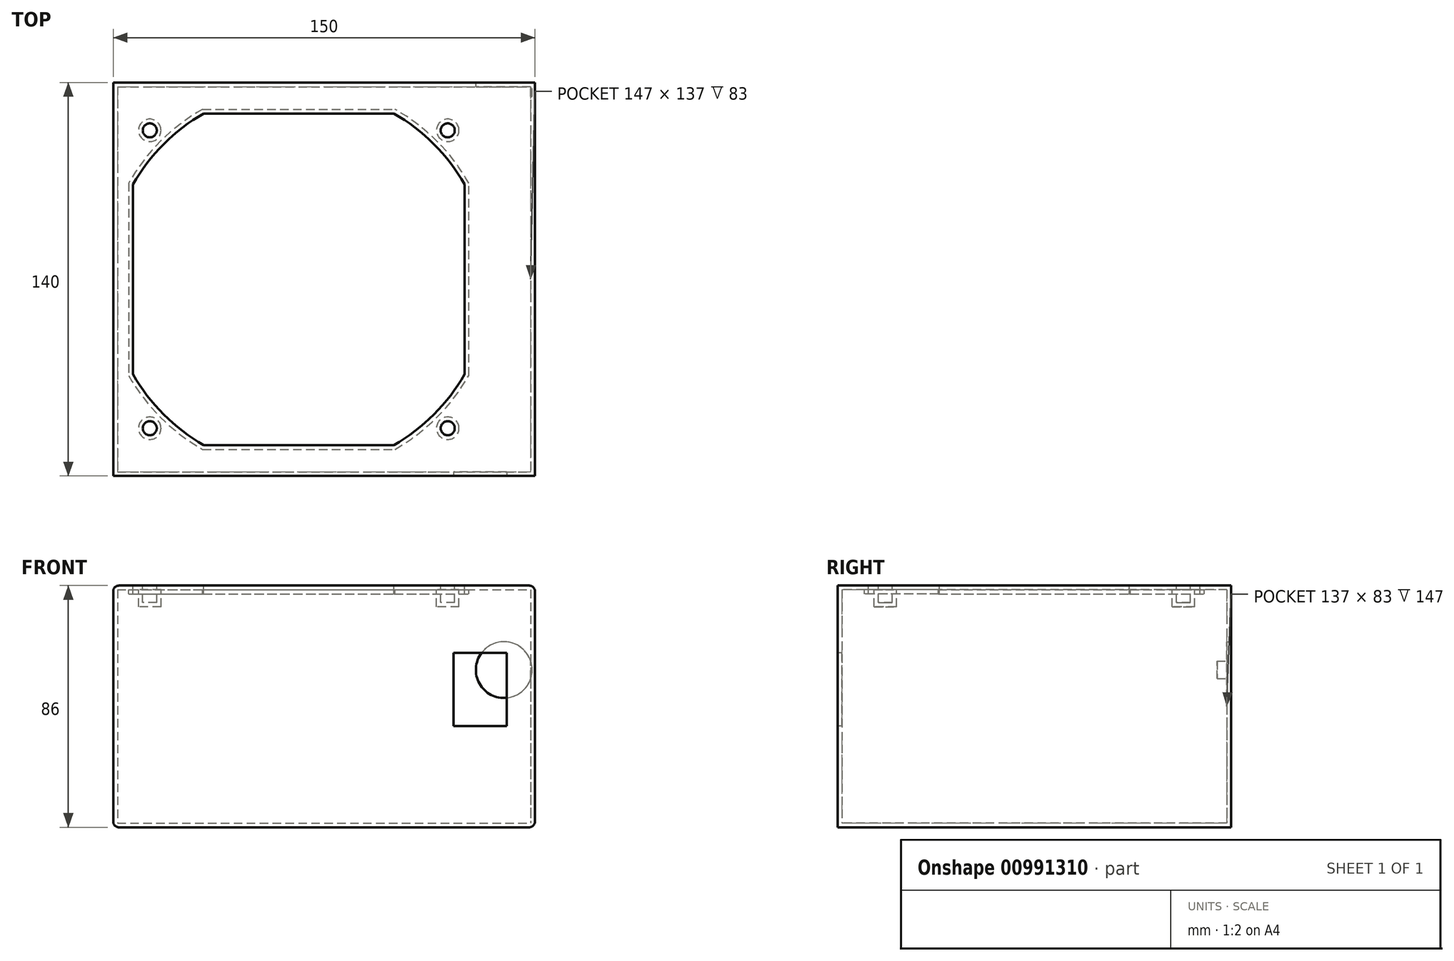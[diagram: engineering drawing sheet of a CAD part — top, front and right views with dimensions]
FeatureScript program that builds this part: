
annotation { "Feature Type Name" : "Feature", "Feature Type Description" : "" }
export const myFeature = defineFeature(function(context is Context, id is Id, definition is map)
    precondition{}
    {
        {
            var Q0;
            Q0=qCreatedBy(makeId("Top.planeOp"),FACE);
            var sketch = newSketch(context, id + "F0", { "sketchPlane" : qUnion([Q0])});
            skLineSegment(sketch, "E0.bottom", {"start": v(-75, 70) * mm, "end": v(75, 70) * mm});
            skLineSegment(sketch, "E0.top", {"start": v(-75, -70) * mm, "end": v(75, -70) * mm});
            skLineSegment(sketch, "E0.left", {"start": v(-75, 70) * mm, "end": v(-75, -70) * mm});
            skLineSegment(sketch, "E0.right", {"start": v(75, 70) * mm, "end": v(75, -70) * mm});
            skPoint(sketch, "E0.middle", {"position": v(0, 0) * mm});
            skSolve(sketch);
        }
        {
            var Q0;
            Q0 = qSketchRegion(id + "F0", true);
            extrude(context, id + "F1", {"entities" : qUnion([Q0]), "depth" : 86 * mm, "offsetDistance" : 25 * mm});
        }
        {
            var Q0;
            Q0=makeQuery(id+"F1.opExtrude","CAP_FACE",FACE,{"disambiguationData":[OSD([sQuery(id+"F0.wireOp",EDGE,"E0.bottom"),sQuery(id+"F0.wireOp",EDGE,"E0.top"),sQuery(id+"F0.wireOp",EDGE,"E0.left"),sQuery(id+"F0.wireOp",EDGE,"E0.right")])],"isStart":false});
            var sketch = newSketch(context, id + "F2", { "sketchPlane" : qUnion([Q0])});
            skCircle(sketch, "E1", {"center": v(44, -53) * mm, "radius": 2.5 * mm});
            skCircle(sketch, "E2", {"center": v(-62, 53) * mm, "radius": 2.5 * mm});
            skCircle(sketch, "E3", {"center": v(44, 53) * mm, "radius": 2.5 * mm});
            skCircle(sketch, "E4", {"center": v(-62, -53) * mm, "radius": 2.5 * mm});
            skLineSegment(sketch, "E5", {"start": v(-9, 0) * mm, "end": v(-62, -53) * mm, "construction": true});
            skArc(sketch, "E6", {"start": v(-42.8, 59) * mm, "mid": v(-57.08, 48.08) * mm, "end": v(-68, 33.8) * mm});
            skArc(sketch, "E7.1.0", {"start": v(-68, -33.8) * mm, "mid": v(-57.08, -48.08) * mm, "end": v(-42.8, -59) * mm});
            skArc(sketch, "E7.2.0", {"start": v(24.8, -59) * mm, "mid": v(39.08, -48.08) * mm, "end": v(50, -33.8) * mm});
            skArc(sketch, "E7.3.0", {"start": v(50, 33.8) * mm, "mid": v(39.08, 48.08) * mm, "end": v(24.8, 59) * mm});
            skLineSegment(sketch, "E8", {"start": v(-68, 33.8) * mm, "end": v(-68, -33.8) * mm});
            skLineSegment(sketch, "E9", {"start": v(-42.8, -59) * mm, "end": v(24.8, -59) * mm});
            skLineSegment(sketch, "E10", {"start": v(50, -33.8) * mm, "end": v(50, 33.8) * mm});
            skLineSegment(sketch, "E11", {"start": v(-42.8, 59) * mm, "end": v(24.8, 59) * mm});
            skSolve(sketch);
        }
        {
            var Q0;
            Q0=makeQuery(id+"F2.imprint","IMPRINT",FACE,{"disambiguationData":[TD([[makeQuery(id+"F2.imprint","IMPRINT",EDGE,{"derivedFrom":sQuery(id+"F2.wireOp",EDGE,"E6")}),1.0]])]});
            extrude(context, id + "F3", {"entities" : qUnion([Q0]), "operationType" : NewBodyOperationType.REMOVE, "oppositeDirection" : true, "depth" : 3 * mm, "offsetDistance" : 25 * mm});
        }
        {
            var Q0;
            Q0=makeQuery(id+"F2.imprint","IMPRINT",FACE,{"disambiguationData":[TD([[makeQuery(id+"F2.imprint","IMPRINT",EDGE,{"derivedFrom":sQuery(id+"F2.wireOp",EDGE,"E2")}),1.0]])]});
            var Q1;
            Q1=makeQuery(id+"F2.imprint","IMPRINT",FACE,{"disambiguationData":[TD([[makeQuery(id+"F2.imprint","IMPRINT",EDGE,{"derivedFrom":sQuery(id+"F2.wireOp",EDGE,"E3")}),1.0]])]});
            var Q2;
            Q2=makeQuery(id+"F2.imprint","IMPRINT",FACE,{"disambiguationData":[TD([[makeQuery(id+"F2.imprint","IMPRINT",EDGE,{"derivedFrom":sQuery(id+"F2.wireOp",EDGE,"E1")}),1.0]])]});
            var Q3;
            Q3=makeQuery(id+"F2.imprint","IMPRINT",FACE,{"disambiguationData":[TD([[makeQuery(id+"F2.imprint","IMPRINT",EDGE,{"derivedFrom":sQuery(id+"F2.wireOp",EDGE,"E4")}),1.0]])]});
            extrude(context, id + "F4", {"entities" : qUnion([Q0, Q1, Q2, Q3]), "operationType" : NewBodyOperationType.REMOVE, "oppositeDirection" : true, "depth" : 6 * mm, "offsetDistance" : 25 * mm});
        }
        {
            var Q0;
            Q0=makeQuery(id+"F3.boolean.opBoolean","COPY",FACE,{"derivedFrom":makeQuery(id+"F3.opExtrude","CAP_FACE",FACE,{"disambiguationData":[OSD([sQuery(id+"F2.wireOp",EDGE,"E6"),sQuery(id+"F2.wireOp",EDGE,"E7.1.0"),sQuery(id+"F2.wireOp",EDGE,"E7.2.0"),sQuery(id+"F2.wireOp",EDGE,"E7.3.0"),sQuery(id+"F2.wireOp",EDGE,"E8"),sQuery(id+"F2.wireOp",EDGE,"E9"),sQuery(id+"F2.wireOp",EDGE,"E10"),sQuery(id+"F2.wireOp",EDGE,"E11")])],"isStart":false})});
            shell(context, id + "F5", {"entities" : qUnion([Q0]), "thickness" : 1.5 * mm});
        }
        {
            var Q0;
            Q0=makeQuery(id+"F1.opExtrude","SWEPT_FACE",FACE,{"disambiguationData":[OSD([sQuery(id+"F0.wireOp",EDGE,"E0.top")])]});
            var sketch = newSketch(context, id + "F6", { "sketchPlane" : qUnion([Q0])});
            skLineSegment(sketch, "E12.bottom", {"start": v(44, 64) * mm, "end": v(67, 64) * mm});
            skLineSegment(sketch, "E12.top", {"start": v(44, 34) * mm, "end": v(67, 34) * mm});
            skLineSegment(sketch, "E12.left", {"start": v(44, 64) * mm, "end": v(44, 34) * mm});
            skLineSegment(sketch, "E12.right", {"start": v(67, 64) * mm, "end": v(67, 34) * mm});
            skPoint(sketch, "E12.middle", {"position": v(55.5, 49) * mm});
            skLineSegment(sketch, "E13.0", {"start": v(46, 62) * mm, "end": v(65, 62) * mm});
            skLineSegment(sketch, "E13.1", {"start": v(46, 62) * mm, "end": v(46, 36) * mm});
            skLineSegment(sketch, "E13.2", {"start": v(46, 36) * mm, "end": v(65, 36) * mm});
            skLineSegment(sketch, "E13.3", {"start": v(65, 62) * mm, "end": v(65, 36) * mm});
            skSolve(sketch);
        }
        {
            var Q0;
            Q0=makeQuery(id+"F6.imprint","IMPRINT",FACE,{"disambiguationData":[TD([[makeQuery(id+"F6.imprint","IMPRINT",EDGE,{"derivedFrom":sQuery(id+"F6.wireOp",EDGE,"E13.0")}),-1.0]])]});
            extrude(context, id + "F7", {"entities" : qUnion([Q0]), "operationType" : NewBodyOperationType.REMOVE, "oppositeDirection" : true, "depth" : 10 * mm, "offsetDistance" : 25 * mm});
        }
        {
            var Q0;
            Q0=makeQuery(id+"F1.opExtrude","SWEPT_FACE",FACE,{"disambiguationData":[OSD([sQuery(id+"F0.wireOp",EDGE,"E0.bottom")])]});
            var sketch = newSketch(context, id + "F8", { "sketchPlane" : qUnion([Q0])});
            skCircle(sketch, "E14", {"center": v(-64, 56) * mm, "radius": 10 * mm});
            skSolve(sketch);
        }
        {
            var Q0;
            Q0=makeQuery(id+"F8.imprint","IMPRINT",FACE,{"disambiguationData":[TD([[makeQuery(id+"F8.imprint","IMPRINT",EDGE,{"derivedFrom":sQuery(id+"F8.wireOp",EDGE,"E14")}),1.0]])]});
            extrude(context, id + "F9", {"entities" : qUnion([Q0]), "operationType" : NewBodyOperationType.REMOVE, "oppositeDirection" : true, "depth" : 5 * mm, "offsetDistance" : 25 * mm});
        }
        {
            var Q0;
            Q0=makeQuery(id+"F1.opExtrude","CAP_EDGE",EDGE,{"disambiguationData":[OSD([sQuery(id+"F0.wireOp",EDGE,"E0.right")])],"isStart":false});
            var Q1;
            Q1=makeQuery(id+"F1.opExtrude","CAP_EDGE",EDGE,{"disambiguationData":[OSD([sQuery(id+"F0.wireOp",EDGE,"E0.right")])],"isStart":true});
            var Q2;
            Q2=makeQuery(id+"F1.opExtrude","CAP_EDGE",EDGE,{"disambiguationData":[OSD([sQuery(id+"F0.wireOp",EDGE,"E0.left")])],"isStart":false});
            var Q3;
            Q3=makeQuery(id+"F1.opExtrude","CAP_EDGE",EDGE,{"disambiguationData":[OSD([sQuery(id+"F0.wireOp",EDGE,"E0.left")])],"isStart":true});
            fillet(context, id + "F10", {"entities" : qUnion([Q0, Q1, Q2, Q3]), "radius" : 2 * mm, "tangentPropagation" : true, "allowEdgeOverflow" : false});
        }
    });
